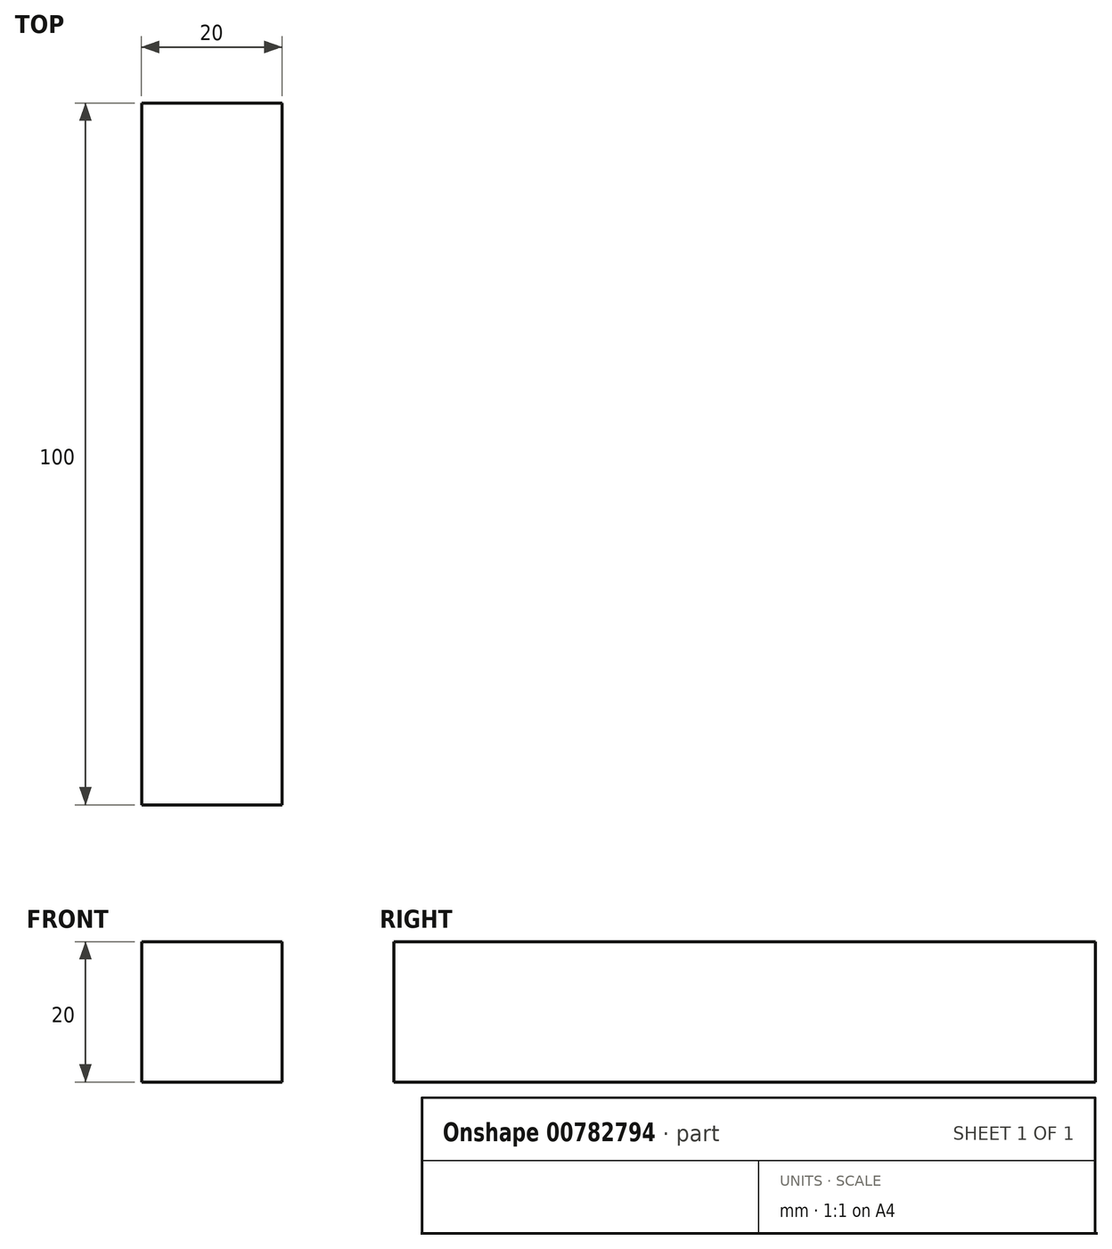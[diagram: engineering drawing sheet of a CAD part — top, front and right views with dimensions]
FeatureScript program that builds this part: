
annotation { "Feature Type Name" : "Feature", "Feature Type Description" : "" }
export const myFeature = defineFeature(function(context is Context, id is Id, definition is map)
    precondition{}
    {
        {
            var Q0;
            Q0=qCreatedBy(makeId("Top.planeOp"),FACE);
            var sketch = newSketch(context, id + "F0", { "sketchPlane" : qUnion([Q0])});
            skLineSegment(sketch, "E0", {"start": v(-77.1, -15.77) * mm, "end": v(-57.1, -15.77) * mm});
            skLineSegment(sketch, "E1", {"start": v(-57.1, -15.77) * mm, "end": v(-57.1, 84.23) * mm});
            skLineSegment(sketch, "E2", {"start": v(-57.1, 84.23) * mm, "end": v(-77.1, 84.23) * mm});
            skLineSegment(sketch, "E3", {"start": v(-77.1, 84.23) * mm, "end": v(-77.1, -15.77) * mm});
            skSolve(sketch);
        }
        {
            var Q0;
            Q0 = qSketchRegion(id + "F0", true);
            extrude(context, id + "F1", {"entities" : qUnion([Q0]), "depth" : 20 * mm, "offsetDistance" : 25 * mm});
        }
    });
